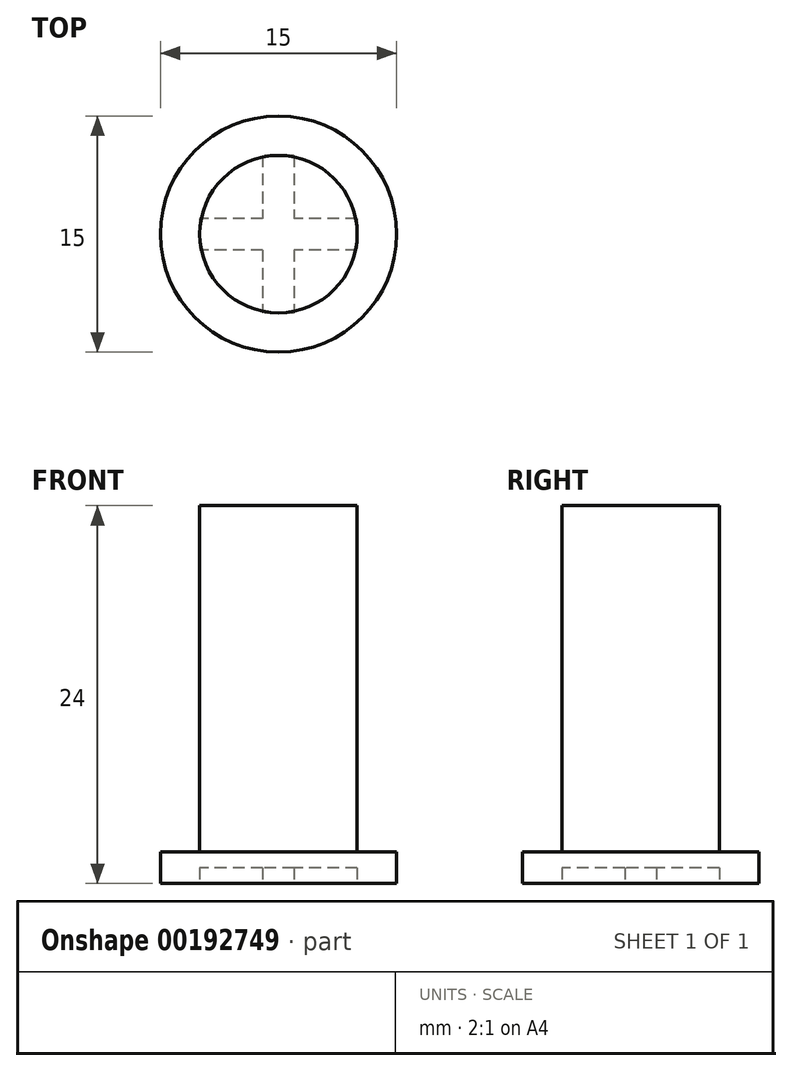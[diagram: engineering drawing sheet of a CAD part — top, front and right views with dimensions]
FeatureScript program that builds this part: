
annotation { "Feature Type Name" : "Feature", "Feature Type Description" : "" }
export const myFeature = defineFeature(function(context is Context, id is Id, definition is map)
    precondition{}
    {
        {
            var Q0;
            Q0=qCreatedBy(makeId("Top.planeOp"),FACE);
            var sketch = newSketch(context, id + "F0", { "sketchPlane" : qUnion([Q0])});
            skCircle(sketch, "E0", {"center": v(0, 0) * mm, "radius": 7.5 * mm});
            skSolve(sketch);
        }
        {
            var Q0;
            Q0=makeQuery(id+"F0.imprint","IMPRINT",FACE,{"disambiguationData":[TD([[makeQuery(id+"F0.imprint","IMPRINT",EDGE,{"derivedFrom":sQuery(id+"F0.wireOp",EDGE,"E0")}),1.0]])]});
            extrude(context, id + "F1", {"entities" : qUnion([Q0]), "depth" : 2 * mm});
        }
        {
            var Q0;
            Q0=makeQuery(id+"F1.opExtrude","CAP_FACE",FACE,{"disambiguationData":[OSD([sQuery(id+"F0.wireOp",EDGE,"E0")])],"isStart":false});
            var sketch = newSketch(context, id + "F2", { "sketchPlane" : qUnion([Q0])});
            skCircle(sketch, "E1", {"center": v(0, 0) * mm, "radius": 5 * mm});
            skSolve(sketch);
        }
        {
            var Q0;
            Q0 = qSketchRegion(id + "F2", true);
            extrude(context, id + "F3", {"entities" : qUnion([Q0]), "operationType" : NewBodyOperationType.ADD, "depth" : 22 * mm});
        }
        {
            var Q0;
            Q0=makeQuery(id+"F1.opExtrude","CAP_FACE",FACE,{"disambiguationData":[OSD([sQuery(id+"F0.wireOp",EDGE,"E0")])],"isStart":true});
            var sketch = newSketch(context, id + "F4", { "sketchPlane" : qUnion([Q0])});
            skLineSegment(sketch, "E2.bottom", {"start": v(5, -1) * mm, "end": v(-5, -1) * mm});
            skLineSegment(sketch, "E2.top", {"start": v(5, 1) * mm, "end": v(-5, 1) * mm});
            skLineSegment(sketch, "E2.left", {"start": v(5, -1) * mm, "end": v(5, 1) * mm});
            skLineSegment(sketch, "E2.right", {"start": v(-5, -1) * mm, "end": v(-5, 1) * mm});
            skPoint(sketch, "E2.middle", {"position": v(0, 0) * mm});
            skLineSegment(sketch, "E3.bottom", {"start": v(1, -5) * mm, "end": v(-1, -5) * mm});
            skLineSegment(sketch, "E3.top", {"start": v(1, 5) * mm, "end": v(-1, 5) * mm});
            skLineSegment(sketch, "E3.left", {"start": v(1, -5) * mm, "end": v(1, 5) * mm});
            skLineSegment(sketch, "E3.right", {"start": v(-1, -5) * mm, "end": v(-1, 5) * mm});
            skSolve(sketch);
        }
        {
            var Q0;
            Q0 = qSketchRegion(id + "F4", true);
            extrude(context, id + "F5", {"entities" : qUnion([Q0]), "operationType" : NewBodyOperationType.REMOVE, "oppositeDirection" : true, "depth" : 1 * mm});
        }
    });
